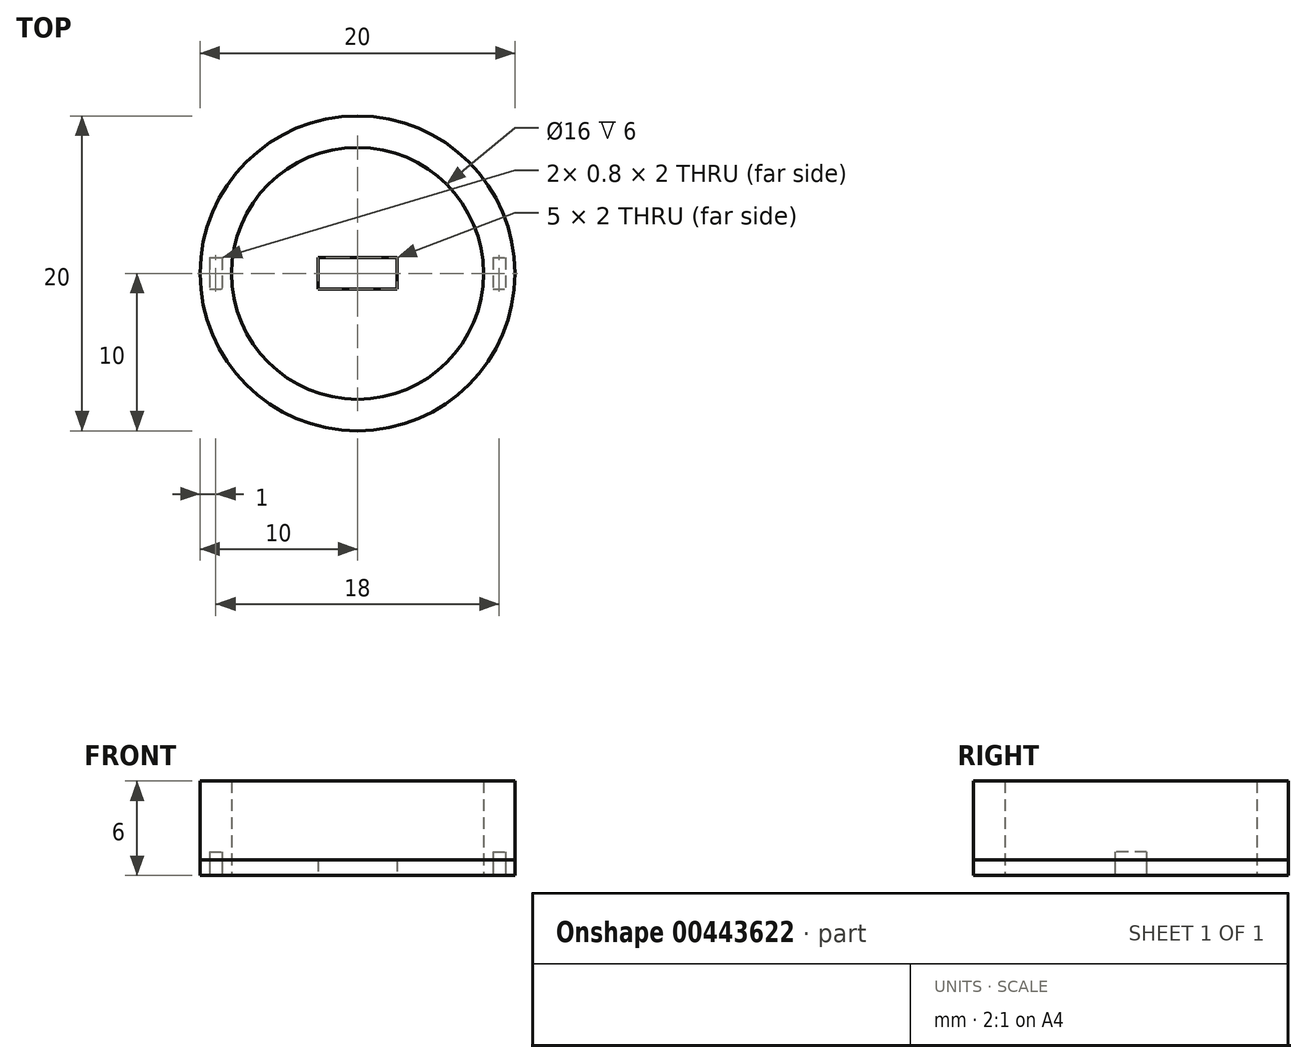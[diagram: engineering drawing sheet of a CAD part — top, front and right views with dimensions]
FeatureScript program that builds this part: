
annotation { "Feature Type Name" : "Feature", "Feature Type Description" : "" }
export const myFeature = defineFeature(function(context is Context, id is Id, definition is map)
    precondition{}
    {
        {
            var Q0;
            Q0=qCreatedBy(makeId("Top.planeOp"),FACE);
            var sketch = newSketch(context, id + "F0", { "sketchPlane" : qUnion([Q0])});
            skCircle(sketch, "E0", {"center": v(0, 0) * mm, "radius": 10 * mm});
            skCircle(sketch, "E1", {"center": v(0, 0) * mm, "radius": 8 * mm});
            skSolve(sketch);
        }
        {
            var Q0;
            Q0 = qSketchRegion(id + "F0", true);
            extrude(context, id + "F1", {"entities" : qUnion([Q0]), "depth" : 6 * mm});
        }
        {
            var Q0;
            Q0=qCreatedBy(makeId("Top.planeOp"),FACE);
            var sketch = newSketch(context, id + "F2", { "sketchPlane" : qUnion([Q0])});
            skCircle(sketch, "E2", {"center": v(0, 0) * mm, "radius": 10 * mm});
            skLineSegment(sketch, "E3.bottom", {"start": v(-9.4, 1) * mm, "end": v(-8.6, 1) * mm});
            skLineSegment(sketch, "E3.top", {"start": v(-9.4, -1) * mm, "end": v(-8.6, -1) * mm});
            skLineSegment(sketch, "E3.left", {"start": v(-9.4, 1) * mm, "end": v(-9.4, -1) * mm});
            skLineSegment(sketch, "E3.right", {"start": v(-8.6, 1) * mm, "end": v(-8.6, -1) * mm});
            skLineSegment(sketch, "E4.bottom", {"start": v(8.6, 1) * mm, "end": v(9.4, 1) * mm});
            skLineSegment(sketch, "E4.top", {"start": v(8.6, -1) * mm, "end": v(9.4, -1) * mm});
            skLineSegment(sketch, "E4.left", {"start": v(8.6, 1) * mm, "end": v(8.6, -1) * mm});
            skLineSegment(sketch, "E4.right", {"start": v(9.4, 1) * mm, "end": v(9.4, -1) * mm});
            skLineSegment(sketch, "E5.bottom", {"start": v(-2.5, 1) * mm, "end": v(2.5, 1) * mm});
            skLineSegment(sketch, "E5.top", {"start": v(-2.5, -1) * mm, "end": v(2.5, -1) * mm});
            skLineSegment(sketch, "E5.left", {"start": v(-2.5, 1) * mm, "end": v(-2.5, -1) * mm});
            skLineSegment(sketch, "E5.right", {"start": v(2.5, 1) * mm, "end": v(2.5, -1) * mm});
            skSolve(sketch);
        }
        {
            var Q0;
            Q0 = qSketchRegion(id + "F2", true);
            extrude(context, id + "F3", {"entities" : qUnion([Q0]), "depth" : 1 * mm});
        }
        {
            var Q0;
            Q0=makeQuery(id+"F2.imprint","IMPRINT",FACE,{"disambiguationData":[TD([[makeQuery(id+"F2.imprint","IMPRINT",EDGE,{"derivedFrom":sQuery(id+"F2.wireOp",EDGE,"E4.bottom")}),-1.0]])]});
            var Q1;
            Q1=makeQuery(id+"F2.imprint","IMPRINT",FACE,{"disambiguationData":[TD([[makeQuery(id+"F2.imprint","IMPRINT",EDGE,{"derivedFrom":sQuery(id+"F2.wireOp",EDGE,"E3.bottom")}),-1.0]])]});
            extrude(context, id + "F4", {"entities" : qUnion([Q0, Q1]), "operationType" : NewBodyOperationType.REMOVE, "depth" : 1.5 * mm});
        }
    });
